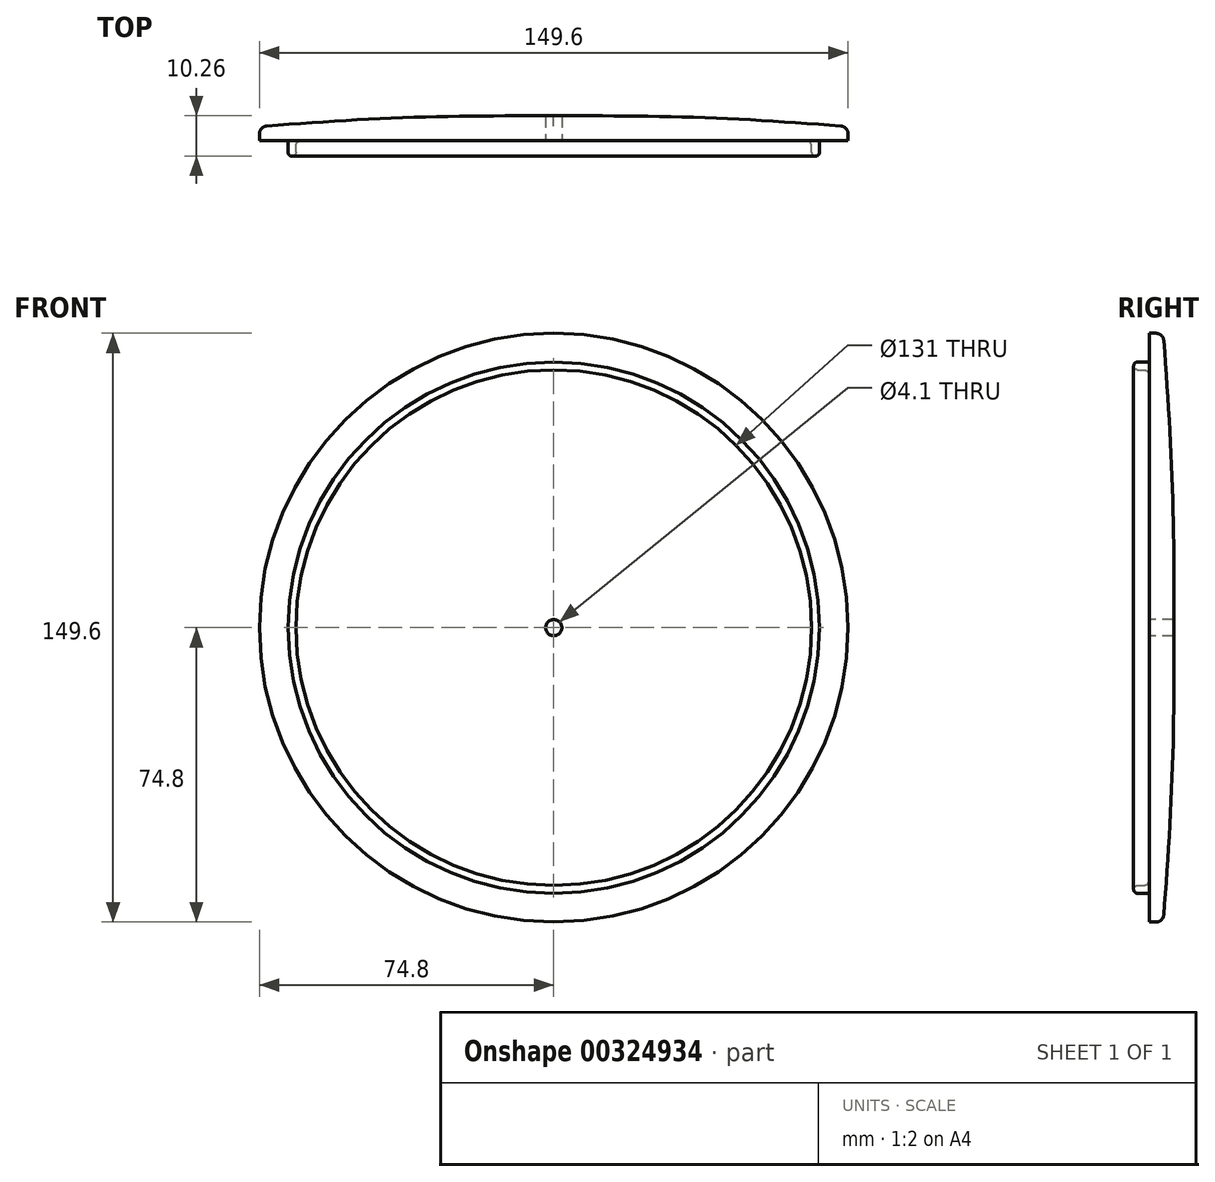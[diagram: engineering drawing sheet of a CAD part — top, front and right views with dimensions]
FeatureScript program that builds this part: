
annotation { "Feature Type Name" : "Feature", "Feature Type Description" : "" }
export const myFeature = defineFeature(function(context is Context, id is Id, definition is map)
    precondition{}
    {
        {
            var Q0;
            Q0=qCreatedBy(makeId("Top.planeOp"),FACE);
            var sketch = newSketch(context, id + "F0", { "sketchPlane" : qUnion([Q0])});
            skFitSpline(sketch, "E0", {"points": [v(-74.8, 0) * mm, v(-36.68, 2.32) * mm, v(0, 2.75) * mm], "startDerivative": vector(68.48, 5.69) * mm, "endDerivative": vector(72.71, -0.16) * mm});
            skLineSegment(sketch, "E1", {"start": v(0, 2.75) * mm, "end": v(0, 0) * mm});
            skLineSegment(sketch, "E2", {"start": v(-74.8, 0) * mm, "end": v(-74.8, -3.5) * mm});
            skLineSegment(sketch, "E3", {"start": v(-74.8, -3.5) * mm, "end": v(0, -3.5) * mm});
            skLineSegment(sketch, "E4", {"start": v(0, -3.5) * mm, "end": v(0, 0) * mm});
            skSolve(sketch);
        }
        {
            var Q0;
            Q0 = qSketchRegion(id + "F0", true);
            var Q1;
            Q1=sQuery(id+"F0.wireOp",EDGE,"E4");
            revolve(context, id + "F1", {"entities" : qUnion([Q0]), "axis" : qUnion([Q1]), "revolveType" : RevolveType.FULL});
        }
        {
            var Q0;
            Q0=makeQuery(id+"F1.opRevolve","SWEPT_FACE",FACE,{"disambiguationData":[OSD([sQuery(id+"F0.wireOp",EDGE,"E3")])]});
            var sketch = newSketch(context, id + "F2", { "sketchPlane" : qUnion([Q0])});
            skCircle(sketch, "E5", {"center": v(0, 0) * mm, "radius": 67.5 * mm});
            skCircle(sketch, "E6", {"center": v(0, 0) * mm, "radius": 65.5 * mm});
            skSolve(sketch);
        }
        {
            var Q0;
            Q0=makeQuery(id+"F2.imprint","IMPRINT",FACE,{"disambiguationData":[TD([[makeQuery(id+"F2.imprint","IMPRINT",EDGE,{"derivedFrom":sQuery(id+"F2.wireOp",EDGE,"E5")}),1.0]])]});
            extrude(context, id + "F3", {"entities" : qUnion([Q0]), "operationType" : NewBodyOperationType.ADD, "depth" : 4 * mm});
        }
        {
            var Q0;
            Q0=makeQuery(id+"F3.opExtrude","CAP_EDGE",EDGE,{"disambiguationData":[OSD([sQuery(id+"F2.wireOp",EDGE,"E6")])],"isStart":false});
            var Q1;
            Q1=makeQuery(id+"F3.opExtrude","CAP_EDGE",EDGE,{"disambiguationData":[OSD([sQuery(id+"F2.wireOp",EDGE,"E5")])],"isStart":false});
            fillet(context, id + "F4", {"entities" : qUnion([Q0, Q1]), "radius" : 1 * mm, "tangentPropagation" : true, "allowEdgeOverflow" : false});
        }
        {
            var Q0;
            Q0=makeQuery(id+"F3.opExtrude","CAP_EDGE",EDGE,{"disambiguationData":[OSD([sQuery(id+"F2.wireOp",EDGE,"E6")])],"isStart":true});
            var Q1;
            Q1=makeQuery(id+"F3.opExtrude","CAP_EDGE",EDGE,{"disambiguationData":[OSD([sQuery(id+"F2.wireOp",EDGE,"E5")])],"isStart":true});
            fillet(context, id + "F5", {"entities" : qUnion([Q0, Q1]), "radius" : 1.5 * mm, "tangentPropagation" : true, "allowEdgeOverflow" : false});
        }
        {
            var Q0;
            Q0=makeQuery(id+"F1.opRevolve","SWEPT_EDGE",EDGE,{"disambiguationData":[OSD([sQuery(id+"F0.wireOp",EDGE,"E0"),sQuery(id+"F0.wireOp",EDGE,"E2")])]});
            fillet(context, id + "F6", {"entities" : qUnion([Q0]), "radius" : 2 * mm, "tangentPropagation" : true, "allowEdgeOverflow" : false});
        }
        {
            var Q0;
            Q0=makeQuery(id+"F3.boolean.opBoolean","SPLIT",FACE,{"disambiguationData":[TD([makeQuery(id+"F3.opExtrude","SWEPT_FACE",FACE,{"disambiguationData":[OSD([sQuery(id+"F2.wireOp",EDGE,"E6")])]})])],"derivedFrom":makeQuery(id+"F1.opRevolve","SWEPT_FACE",FACE,{"disambiguationData":[OSD([sQuery(id+"F0.wireOp",EDGE,"E3")])]})});
            var sketch = newSketch(context, id + "F7", { "sketchPlane" : qUnion([Q0])});
            skCircle(sketch, "E7", {"center": v(0, 0) * mm, "radius": 2.05 * mm});
            skSolve(sketch);
        }
        {
            var Q0;
            Q0 = qSketchRegion(id + "F7", true);
            extrude(context, id + "F8", {"entities" : qUnion([Q0]), "operationType" : NewBodyOperationType.REMOVE, "endBound" : BoundingType.THROUGH_ALL, "oppositeDirection" : true, "depth" : 25 * mm});
        }
    });
